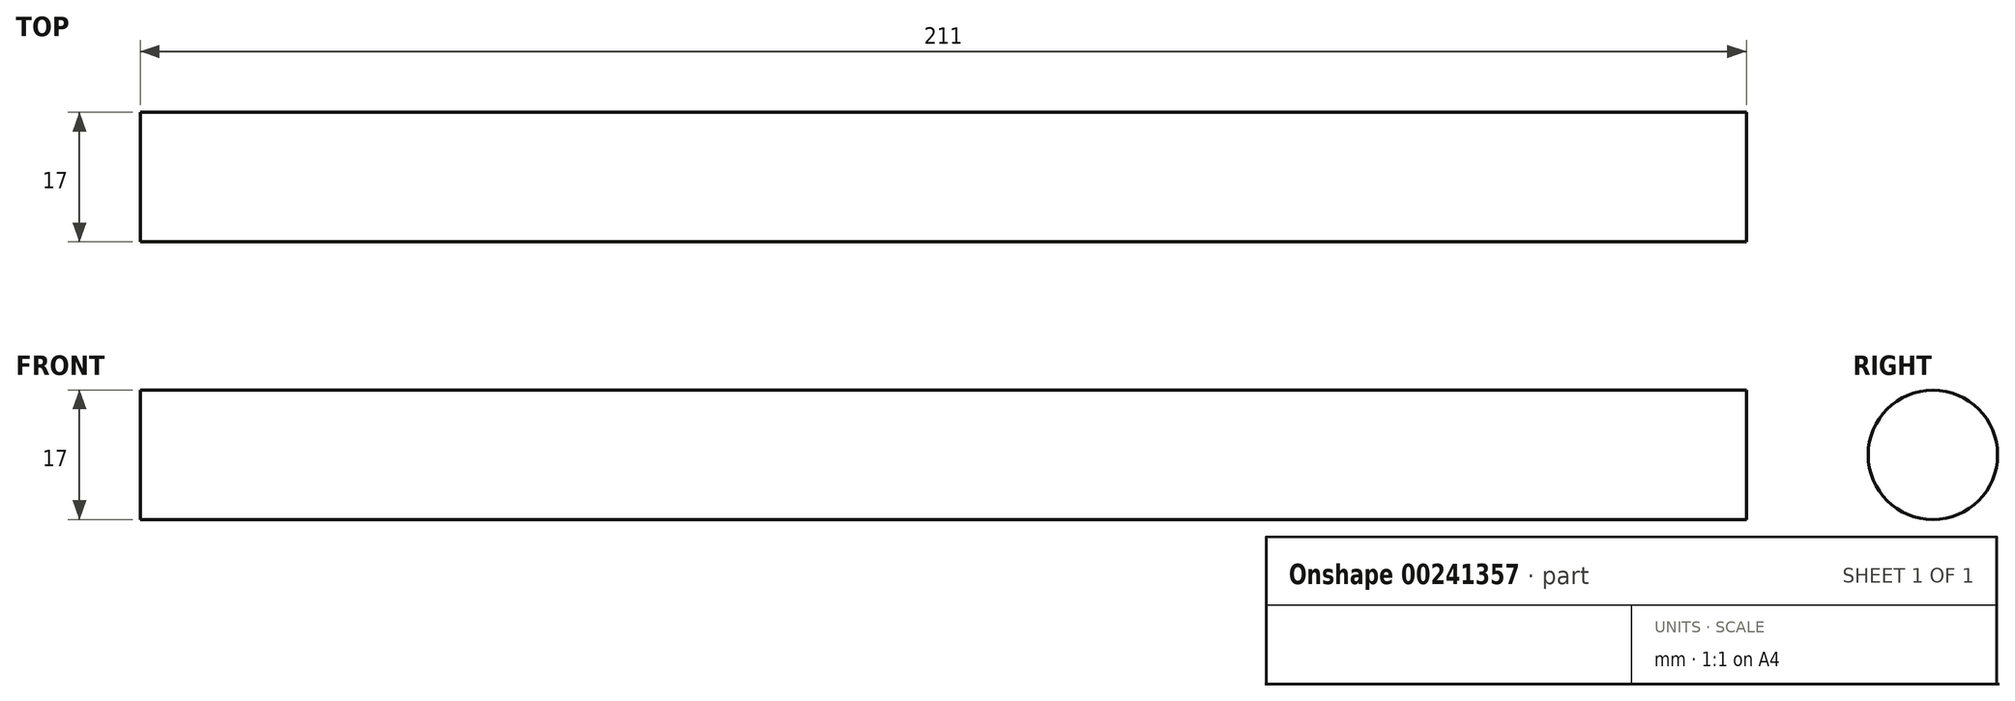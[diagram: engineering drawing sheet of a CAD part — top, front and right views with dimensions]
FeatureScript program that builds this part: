
annotation { "Feature Type Name" : "Feature", "Feature Type Description" : "" }
export const myFeature = defineFeature(function(context is Context, id is Id, definition is map)
    precondition{}
    {
        {
            var Q0;
            Q0=qCreatedBy(makeId("Right.planeOp"),FACE);
            var sketch = newSketch(context, id + "F0", { "sketchPlane" : qUnion([Q0])});
            skCircle(sketch, "E0", {"center": v(0, 0) * mm, "radius": 8.5 * mm});
            skSolve(sketch);
        }
        {
            var Q0;
            Q0 = qSketchRegion(id + "F0", true);
            extrude(context, id + "F1", {"entities" : qUnion([Q0]), "endBound" : BoundingType.SYMMETRIC, "depth" : 211 * mm});
        }
    });
